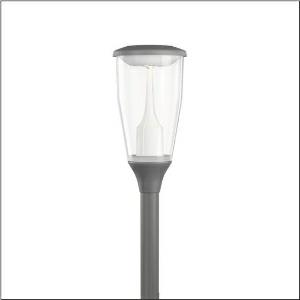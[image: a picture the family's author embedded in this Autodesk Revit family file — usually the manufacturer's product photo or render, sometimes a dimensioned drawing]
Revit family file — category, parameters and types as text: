
# Revit family: dl_11_iq___st1_2a_5xa5565af14hp00022_6a76
name_source: partatom
category: Lighting Fixtures
units: mm (PartAtom-declared; Revit-internal decimal feet)

## family parameters
Cut with Voids When Loaded = No
Host = Face
Light Source = No
Part Type = Normal
Room Calculation Point = No
Round Connector Dimension = Use Diameter
Shared = No

## types (1)
- --- (1 x LED, 4000 lm, 33.6 W, 2200K)
    Apparent Load = 34 VA
    CIE Flux Codes = 23 60 93 95 100
    Color Rendering = 70
    Color Temperature = 2200K
    Default Elevation = 1800 mm
    Description = DL 11 iQ, mast luminaire, Module 540 iQ-SR, primary light control with 3 zone facetted reflector, of plastic, silver coated, highly specular, structured, primary optical cover: cover, of PMMA, transparent, light distribution: ST1.2a, light emission: direct distribution, primary light characteristic: asymmetric, installation type: post-top, LED, High Power LED, light colour: 722, colour temperature: 2200K, control gear: iQ Street-Remote, control: Street-Remote, Auto-Match, Temp-Guard, Lumen-Switch, Night-Set, Smart-Wire, Light-Fading, Desk-Remote (wireless, voltage-free reading and setting of iQ features in the workshop via application-optimized NFC function/RFID function), optimised constant luminous flux control (CLO 2.0), mains connection: 220..240V, AC, 50/60Hz, connection cable pre-assembled, cable length: 5,5m, luminaire housing, upper part, of diecast aluminium, coated, SITECO metallic grey (DB 702S), spigot size: 60mm (post-top), mounting height: 3..5m, post-top mast mounting element, of diecast aluminium, coated, SITECO metallic grey (DB 702S), Module 540 iQ-SR, traffic white (RAL 9016), equipment: Power, protection rating (complete): IP66, insulation class (complete): insulation class II (safety insulation), certification: CE, ENEC, ENEC+, VDE, impact resistance: IK07, packaging unit: 1 piece

Light Distribution: ST1.2a
    Height = 665 mm
    Lamp = 1 x LED
    Lamp Light Flux = 4000 lm
    Lamp Power = 33.6 W
    Lamp count = 1
    Length = 334 mm
    Luminous efficacy = 119 lm/W
    Manufacturer = Siteco
    ModVariant = No
    Model = 5XA5565AF14HP00022
    Number of Poles = 1
    OnlyDefault = Yes
    Power Factor = 1
    Product Name = DL 11 iQ | ST1.2a
    Product group = mast luminaire | pylon top
    ProductGroupID = 6100
    Protection Class = Protection class II
    Protection Degree = IP 66
    RLX_Detail_Level = 1
    RLX_Emergency_Light_Flux = 0 lm
    RLX_Emergency_Type = 0
    RLX_Emergency_Type_DB = No
    RlxData = <blob elided: 155089 chars, md5=19f13128>
    Socket = socket
    Standby Power = 0 W
    System Light Flux = 4000 lm
    System Power = 34 W
    Type Comments = factory setting: luminous flux: 100 % | dim-lin: 254 | 695 mA
    Type Image = l_1258354.jpg
    URL = http://relux.com
    VarID = @adj_040349
    Voltage = 0 V
    Weight = 0.00 kg
    Width = 0 mm  [stored 0 ft]

note: [stored X ft] marks values corroborated as IEEE doubles in the binary element streams (Revit-internal decimal feet)

## geometry (parser evidence)
native form markers: Blend x4, Sweep x13
no freeform markers — native parametric forms only
